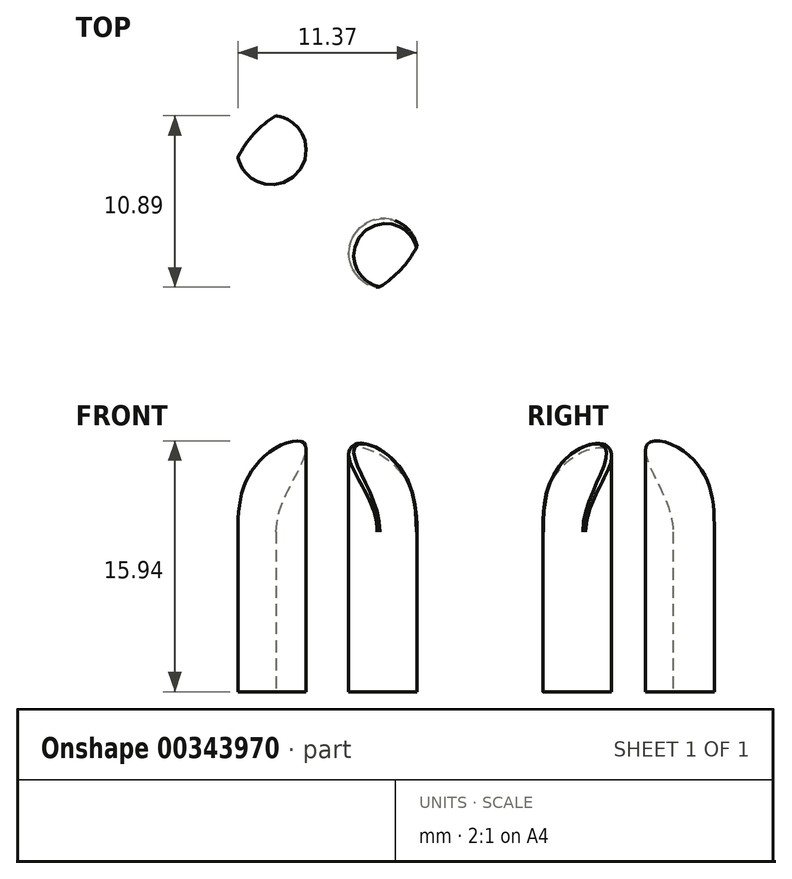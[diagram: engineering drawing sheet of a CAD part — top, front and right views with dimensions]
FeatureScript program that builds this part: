
annotation { "Feature Type Name" : "Feature", "Feature Type Description" : "" }
export const myFeature = defineFeature(function(context is Context, id is Id, definition is map)
    precondition{}
    {
        {
            var Q0;
            Q0=qCreatedBy(makeId("Right.planeOp"),FACE);
            var sketch = newSketch(context, id + "F0", { "sketchPlane" : qUnion([Q0])});
            skLineSegment(sketch, "E0.bottom", {"start": v(0, 0) * mm, "end": v(-6.35, 0) * mm});
            skLineSegment(sketch, "E0.top", {"start": v(0, 16.51) * mm, "end": v(0, 16.51) * mm});
            skLineSegment(sketch, "E0.left", {"start": v(0, 0) * mm, "end": v(0, 16.51) * mm});
            skLineSegment(sketch, "E0.right", {"start": v(-6.35, 0) * mm, "end": v(-6.35, 10.16) * mm});
            skPoint(sketch, "E1.visualSharp", {"position": v(-6.35, 16.51) * mm});
            skArc(sketch, "E1.filletArc", {"start": v(0, 16.51) * mm, "mid": v(-4.5, 14.65) * mm, "end": v(-6.35, 10.16) * mm});
            skSolve(sketch);
        }
        {
            var Q0;
            Q0=makeQuery(id+"F0.imprint","IMPRINT",FACE,{"disambiguationData":[TD([[makeQuery(id+"F0.imprint","IMPRINT",EDGE,{"derivedFrom":sQuery(id+"F0.wireOp",EDGE,"E0.bottom")}),-1.0]])]});
            var Q1;
            Q1=sQuery(id+"F0.wireOp",EDGE,"E0.left");
            revolve(context, id + "F1", {"entities" : qUnion([Q0]), "axis" : qUnion([Q1]), "revolveType" : RevolveType.FULL});
        }
        {
            var Q0;
            Q0=makeQuery(id+"F1.opRevolve","SWEPT_FACE",FACE,{"disambiguationData":[OSD([sQuery(id+"F0.wireOp",EDGE,"E0.bottom")])]});
            var sketch = newSketch(context, id + "F2", { "sketchPlane" : qUnion([Q0])});
            skArc(sketch, "E2", {"start": v(-5.7, 2.82) * mm, "mid": v(-1.93, 1.78) * mm, "end": v(-3.26, 5.45) * mm});
            skArc(sketch, "E3.MirrorCS", {"start": v(5.7, 2.82) * mm, "mid": v(1.93, 1.78) * mm, "end": v(3.26, 5.45) * mm});
            skArc(sketch, "E4.MirrorCS", {"start": v(5.7, -2.82) * mm, "mid": v(1.93, -1.78) * mm, "end": v(3.26, -5.45) * mm});
            skArc(sketch, "E5.MirrorCS", {"start": v(-5.7, -2.82) * mm, "mid": v(-1.93, -1.78) * mm, "end": v(-3.26, -5.45) * mm});
            skSolve(sketch);
        }
        {
            var Q0;
            {var subQ0=sQuery(id+"F2.wireOp",EDGE,"E2");Q0=makeQuery(id+"F2.imprint","IMPRINT",FACE,{"disambiguationData":[TD([[makeQuery(id+"F2.imprint","IMPRINT",EDGE,{"derivedFrom":subQ0}),1.0]])]});}
            var Q1;
            {var subQ0=sQuery(id+"F2.wireOp",EDGE,"E3.MirrorCS");Q1=makeQuery(id+"F2.imprint","IMPRINT",FACE,{"disambiguationData":[TD([[makeQuery(id+"F2.imprint","IMPRINT",EDGE,{"derivedFrom":subQ0}),-1.0]])]});}
            var Q2;
            {var subQ0=sQuery(id+"F2.wireOp",EDGE,"E4.MirrorCS");Q2=makeQuery(id+"F2.imprint","IMPRINT",FACE,{"disambiguationData":[TD([[makeQuery(id+"F2.imprint","IMPRINT",EDGE,{"derivedFrom":subQ0}),1.0]])]});}
            var Q3;
            {var subQ0=sQuery(id+"F2.wireOp",EDGE,"E5.MirrorCS");Q3=makeQuery(id+"F2.imprint","IMPRINT",FACE,{"disambiguationData":[TD([[makeQuery(id+"F2.imprint","IMPRINT",EDGE,{"derivedFrom":subQ0}),-1.0]])]});}
            extrude(context, id + "F3", {"entities" : qUnion([Q0, Q1, Q2, Q3]), "operationType" : NewBodyOperationType.REMOVE, "endBound" : BoundingType.THROUGH_ALL, "oppositeDirection" : true, "depth" : 25.4 * mm});
        }
        {
            var Q0;
            {var subQ0=sQuery(id+"F2.wireOp",EDGE,"E2");var subQ1=sQuery(id+"F0.wireOp",EDGE,"E0.right");var subQ2=sQuery(id+"F0.wireOp",EDGE,"E0.bottom");Q0=makeQuery(id+"F3.boolean.opBoolean","COPY",EDGE,{"derivedFrom":makeQuery(id+"F3.opExtrude","SWEPT_EDGE",EDGE,{"disambiguationData":[OSD([subQ2,subQ1,subQ0]),TDD([makeQuery(id+"F2.imprint","INTERSECT",VERTEX,{"disambiguationData":[OD(0.0)],"derivedFrom":[makeQuery(id+"F1.opRevolve","SWEPT_EDGE",EDGE,{"disambiguationData":[OSD([subQ2,subQ1])]}),subQ0]})])]})});}
            var Q1;
            {var subQ0=sQuery(id+"F2.wireOp",EDGE,"E3.MirrorCS");var subQ1=sQuery(id+"F0.wireOp",EDGE,"E0.right");var subQ2=sQuery(id+"F0.wireOp",EDGE,"E0.bottom");Q1=makeQuery(id+"F3.boolean.opBoolean","COPY",EDGE,{"derivedFrom":makeQuery(id+"F3.opExtrude","SWEPT_EDGE",EDGE,{"disambiguationData":[OSD([subQ2,subQ1,subQ0]),TDD([makeQuery(id+"F2.imprint","INTERSECT",VERTEX,{"disambiguationData":[OD(1.0)],"derivedFrom":[makeQuery(id+"F1.opRevolve","SWEPT_EDGE",EDGE,{"disambiguationData":[OSD([subQ2,subQ1])]}),subQ0]})])]})});}
            var Q2;
            {var subQ0=sQuery(id+"F2.wireOp",EDGE,"E4.MirrorCS");var subQ1=sQuery(id+"F0.wireOp",EDGE,"E0.right");var subQ2=sQuery(id+"F0.wireOp",EDGE,"E0.bottom");Q2=makeQuery(id+"F3.boolean.opBoolean","COPY",EDGE,{"derivedFrom":makeQuery(id+"F3.opExtrude","SWEPT_EDGE",EDGE,{"disambiguationData":[OSD([subQ2,subQ1,subQ0]),TDD([makeQuery(id+"F2.imprint","INTERSECT",VERTEX,{"disambiguationData":[OD(1.0)],"derivedFrom":[makeQuery(id+"F1.opRevolve","SWEPT_EDGE",EDGE,{"disambiguationData":[OSD([subQ2,subQ1])]}),subQ0]})])]})});}
            var Q3;
            {var subQ0=sQuery(id+"F2.wireOp",EDGE,"E5.MirrorCS");var subQ1=sQuery(id+"F0.wireOp",EDGE,"E0.right");var subQ2=sQuery(id+"F0.wireOp",EDGE,"E0.bottom");Q3=makeQuery(id+"F3.boolean.opBoolean","COPY",EDGE,{"derivedFrom":makeQuery(id+"F3.opExtrude","SWEPT_EDGE",EDGE,{"disambiguationData":[OSD([subQ2,subQ1,subQ0]),TDD([makeQuery(id+"F2.imprint","INTERSECT",VERTEX,{"disambiguationData":[OD(1.0)],"derivedFrom":[makeQuery(id+"F1.opRevolve","SWEPT_EDGE",EDGE,{"disambiguationData":[OSD([subQ2,subQ1])]}),subQ0]})])]})});}
            fillet(context, id + "F4", {"entities" : qUnion([Q0, Q1, Q2, Q3]), "radius" : 0.25 * mm, "tangentPropagation" : true, "allowEdgeOverflow" : false});
        }
    });
